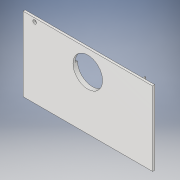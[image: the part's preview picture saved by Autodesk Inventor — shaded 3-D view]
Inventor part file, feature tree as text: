
AUTODESK INVENTOR PART (.ipt)
format: ipt  version: 2019 (Build 230136000, 136)  size: 193,536 bytes
history: native  units: mm
features: extrude x8, sketch x8, fillet x2
ambient origin geometry x8: Origin, YZ Plane, XZ Plane, XY Plane, X Axis, Y Axis, Z Axis, Center Point
bodies: Solid1 (feature_tree)
feature tree (18):
  extrude  "Extrusion1"  Depth=400.0mm
  extrude  "Extrusion2"  Depth=12.0mm
  extrude  "Extrusion3"  Depth=5.0mm
  extrude  "Extrusion4"  Depth=5.0mm
  extrude  "Extrusion5"  Depth=12.0mm
  extrude  "Extrusion6"  Depth=700.0mm
  extrude  "Extrusion7"  Depth=5.0mm TaperAngle=0.0deg
  fillet  "Fillet1"  Radius=5.0mm
  fillet  "Fillet2"  Radius=5.0mm
  extrude  "Extrusion8"  Depth=2.5mm
  sketch  "Sketch1"  dims[d0=700.0mm d1=400.0mm]
  sketch  "Sketch2"  dims[d2=12.0mm d3=0.0mm d4=160.0mm]
  sketch  "Sketch3"  dims[d5=12.0mm d6=0.0mm d7=5.0mm]
  sketch  "Sketch4"  dims[d8=200.0mm d9=5.0mm]
  sketch  "Sketch5"  dims[d10=12.0mm d11=0.0mm d12=90.0mm]
  sketch  "Sketch6"  dims[d13=700.0mm d14=0.0mm d15=90.0mm]
  sketch  "Sketch7"  dims[d16=10000.0mm d17=0.0mm d18=500.0mm d19=0.0mm d20=5.0mm d21=5.0mm]
  sketch  "Sketch8"  dims[d22=7.0mm d23=0.0mm d24=2.5mm d25=0.1mm d26=20.0mm d27=20.0mm d28=0.0mm]
